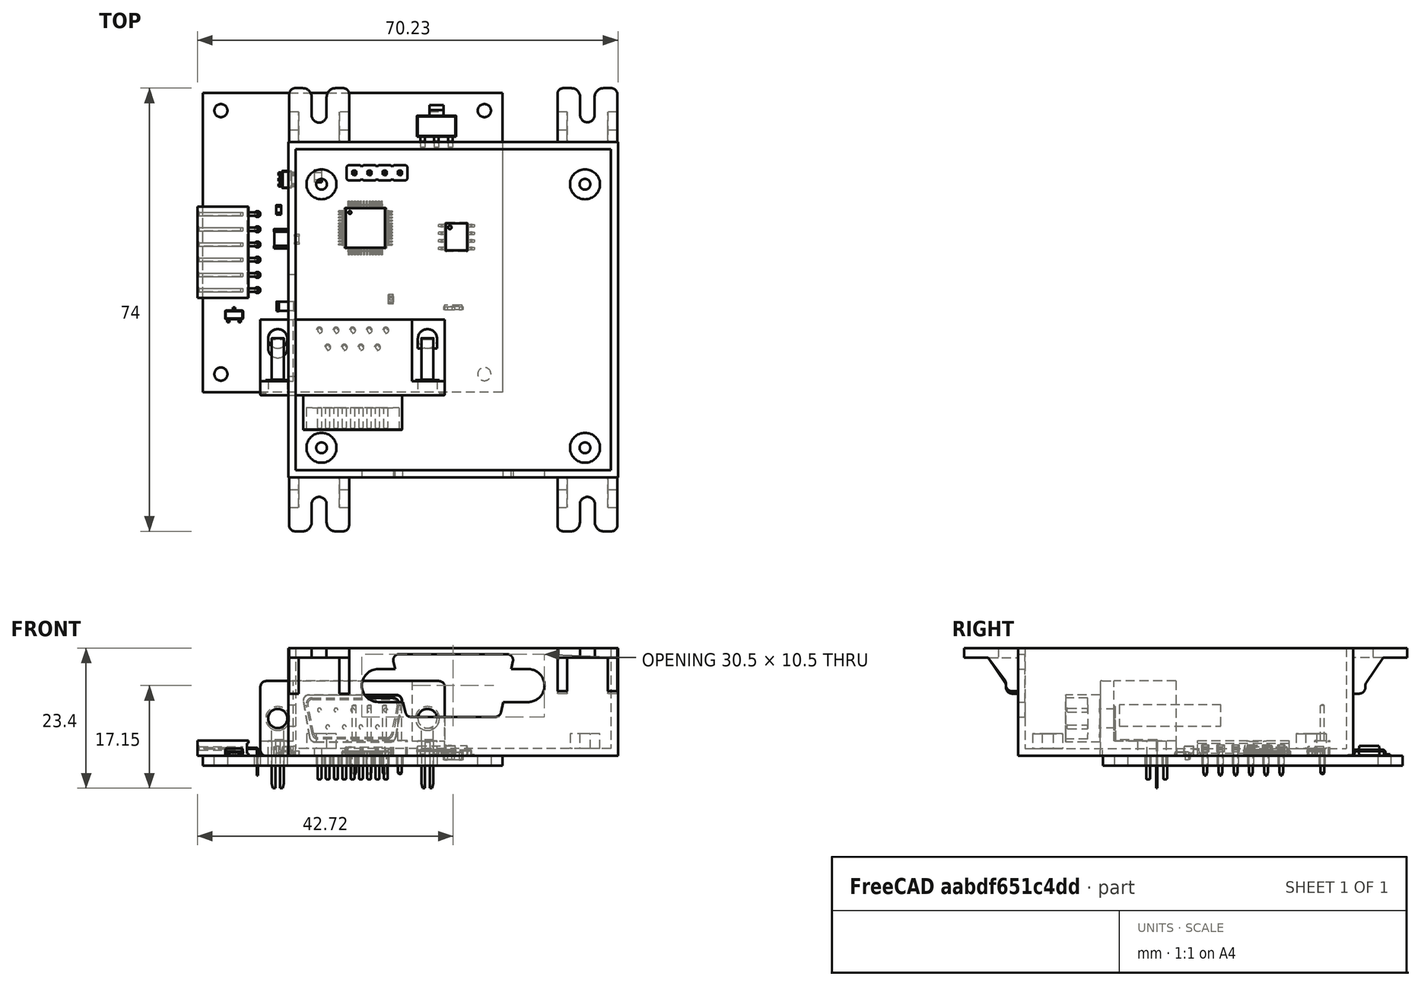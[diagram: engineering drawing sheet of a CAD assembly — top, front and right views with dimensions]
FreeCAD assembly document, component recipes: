
FREECAD ASSEMBLY — COMPONENT RECIPES ("CentralBox")

This assembly document has 6 components, labeled P0..P5 below (a component is one placed body or linked part). 5 of them carry a construction recipe — the FreeCAD feature program that regenerates the part from scratch, quoted from this document or its linked companion documents; the rest are supplied as boundary geometry only. No exploded tour is included for this assembly.
COMPONENT P0 — geometry summary ("CTB-01.kicad_pro"; no construction recipe available for this part):
  bounding box: 56.3 x 50.9 x 17.9 mm
  tessellated surface: 83,718 triangles
  volume: 7836 mm^3 (15% of its bounding box)
COMPONENT P1 — recipe-attached ("Body", modeled in this document).
Construction recipe (the document's own serialized feature program — sketch geometry with constraints, then the solid features built on it; lengths are millimeters unless a unit is written):

FEATURE [Sketcher::SketchObject] Sketch
  FullyConstrained = true
  MapMode = 2
  Support = -> [XY_Plane]
  expr: Constraints[8] = <<Params>>.box_width_external
  expr: Constraints[9] = <<Params>>.box_length_external
  sketch-geometry (4):
    g0: LineSegment StartX=-27.5 StartY=28 StartZ=0 EndX=27.5 EndY=28 EndZ=0
    g1: LineSegment StartX=27.5 StartY=28 StartZ=0 EndX=27.5 EndY=-28 EndZ=0
    g2: LineSegment StartX=27.5 StartY=-28 StartZ=0 EndX=-27.5 EndY=-28 EndZ=0
    g3: LineSegment StartX=-27.5 StartY=-28 StartZ=0 EndX=-27.5 EndY=28 EndZ=0
  constraints (10):
    c: Coincident(g0,g1)
    c: Coincident(g1,g2)
    c: Coincident(g2,g3)
    c: Coincident(g3,g0)
    c: Horizontal(g2)
    c: Vertical(g3)
    c: Symmetric(g0,g1,g-1)
    c: Symmetric(g0,g0,g-2)
    c: DistanceY(g2,g0) = 56
    c: DistanceX(g0,g0) = 55
FEATURE [PartDesign::Pad] Pad
  Direction = (0,0,1)
  Length = 18
  Length2 = 10
  Profile = -> Sketch
  ReferenceAxis = -> Sketch [N_Axis]
  Type = 0
  expr: Length = <<Params>>.box_height
FEATURE [Sketcher::SketchObject] Sketch012
  FullyConstrained = true
  MapMode = 5
  Placement = pos=(0,0,18) rot=(0,0,1;0rad)
  Support = -> [Pad]
  expr: Constraints[8] = <<Params>>.box_length_internal
  expr: Constraints[9] = <<Params>>.box_width_internal
  sketch-geometry (4):
    g0: LineSegment StartX=-26.3 StartY=26.8 StartZ=0 EndX=26.3 EndY=26.8 EndZ=0
    g1: LineSegment StartX=26.3 StartY=26.8 StartZ=0 EndX=26.3 EndY=-26.8 EndZ=0
    g2: LineSegment StartX=26.3 StartY=-26.8 StartZ=0 EndX=-26.3 EndY=-26.8 EndZ=0
    g3: LineSegment StartX=-26.3 StartY=-26.8 StartZ=0 EndX=-26.3 EndY=26.8 EndZ=0
  constraints (10):
    c: Coincident(g0,g1)
    c: Coincident(g1,g2)
    c: Coincident(g2,g3)
    c: Coincident(g3,g0)
    c: Horizontal(g2)
    c: Vertical(g1)
    c: Symmetric(g0,g0,g-2)
    c: Symmetric(g0,g2,g-1)
    c: DistanceX(g0,g0) = 52.6
    c: DistanceY(g2,g0) = 53.6
FEATURE [PartDesign::Pocket] Pocket
  BaseFeature = -> Pad
  Direction = (0,0,-1)
  Length = 16.8
  Length2 = 5
  Profile = -> Sketch012
  ReferenceAxis = -> Sketch012 [N_Axis]
  Type = 0
  expr: Length = <<Params>>.box_depth
FEATURE [PartDesign::SubShapeBinder] Binder
  BindCopyOnChange = 0
  BindMode = 0
  ClaimChildren = false
  Context = -> Body [Binder.]
  Fuse = false
  MakeFace = true
  OffsetFill = false
  OffsetIntersection = false
  OffsetJoinType = 0
  OffsetOpenResult = false
  PartialLoad = false
  Relative = true
  Support = -> [Board_1da8[Step_Models_1da8.Top_1da8.Shape011.Face27]]
  _Version = 2
FEATURE [Sketcher::SketchObject] Sketch013
  ExternalGeometry = -> [Binder]
  FullyConstrained = true
  MapMode = 5
  Placement = pos=(0,-28,0) rot=(1,0,0;1.5708rad)
  Support = -> [Pocket]
  sketch-geometry (17):
    g0: ArcOfCircle CenterX=12.49 CenterY=11.75 CenterZ=0 NormalX=0 NormalY=0 NormalZ=1 AngleXU=0 Radius=2.75 StartAngle=4.70512 EndAngle=7.85398
    g1: ArcOfCircle CenterX=-12.51 CenterY=11.75 CenterZ=0 NormalX=0 NormalY=0 NormalZ=1 AngleXU=0 Radius=2.75 StartAngle=1.5708 EndAngle=4.71239
    g2: LineSegment StartX=-12.51 StartY=9 StartZ=0 EndX=-8.39 EndY=9 EndZ=0
    g3: LineSegment StartX=-12.51 StartY=14.5 StartZ=0 EndX=-9.68 EndY=14.5 EndZ=0
    g4: LineSegment StartX=-12.51 StartY=11.75 StartZ=0 EndX=12.49 EndY=11.75 EndZ=0
    g5: ArcOfCircle CenterX=-9.01 CenterY=16 CenterZ=0 NormalX=0 NormalY=0 NormalZ=1 AngleXU=0 Radius=1 StartAngle=1.5708 EndAngle=3.37594
    g6: ArcOfCircle CenterX=8.99 CenterY=16 CenterZ=0 NormalX=0 NormalY=0 NormalZ=1 AngleXU=0 Radius=1 StartAngle=6.04884 EndAngle=7.85398
    g7: ArcOfCircle CenterX=6.99 CenterY=7.5 CenterZ=0 NormalX=0 NormalY=0 NormalZ=1 AngleXU=0 Radius=1 StartAngle=4.71239 EndAngle=6.06326
    g8: ArcOfCircle CenterX=-7.01 CenterY=7.5 CenterZ=0 NormalX=0 NormalY=0 NormalZ=1 AngleXU=0 Radius=1 StartAngle=3.37255 EndAngle=4.71239
    g9: LineSegment StartX=-9.01 StartY=17 StartZ=0 EndX=8.99 EndY=17 EndZ=0
    g10: LineSegment StartX=6.99 StartY=6.5 StartZ=0 EndX=-7.01 EndY=6.5 EndZ=0
    g11: LineSegment StartX=-7.98345 StartY=7.27109 StartZ=0 EndX=-8.39 EndY=9 EndZ=0
    g12: LineSegment StartX=7.96591 StartY=7.28184 StartZ=0 EndX=8.35 EndY=9 EndZ=0
    g13: LineSegment StartX=9.66 StartY=14.5 StartZ=0 EndX=12.49 EndY=14.5 EndZ=0
    g14: LineSegment StartX=-9.68 StartY=14.5 StartZ=0 EndX=-9.98267 EndY=15.7678 EndZ=0
    g15: LineSegment StartX=8.35 StartY=9 StartZ=0 EndX=12.47 EndY=9.00007 EndZ=0
    g16: LineSegment StartX=9.66 StartY=14.5 StartZ=0 EndX=9.96267 EndY=15.7678 EndZ=0
  constraints (44):
    c: Coincident(g0,g-4)
    c: Coincident(g1,g-3)
    c: Diameter(g1) = 5.5
    c: Equal(g1,g0)
    c: Coincident(g4,g1)
    c: Coincident(g4,g0)
    c: Diameter(g6) = 2
    c: Equal(g6,g5)
    c: Equal(g5,g8)
    c: Equal(g8,g7)
    c: Horizontal(g9)
    c: Horizontal(g10)
    c: DistanceY(g10,g9) = 10.5
    c: DistanceX(g5,g6) = 18
    c: DistanceX(g8,g7) = 14
    c: DistanceX(g7,g0) = 5.5
    c: DistanceY(g7,g0) = 4.25
    c: DistanceX(g6,g0) = 3.5
    c: Tangent(g5,g9) = 1.5708
    c: Tangent(g6,g9) = 1.5708
    c: Tangent(g7,g12) = -1.5708
    c: Tangent(g7,g10) = 1.5708
    c: Tangent(g8,g10) = 1.5708
    c: Tangent(g8,g11) = 1.5708
    c: Tangent(g1,g3) = 1.5708
    c: Tangent(g1,g2) = -1.5708
    c: Coincident(g0,g15) = -1.5708
    c: Coincident(g0,g13) = 1.5708
    c: Coincident(g14,g3)
    c: Coincident(g2,g11)
    c: Coincident(g16,g13)
    c: Coincident(g12,g15)
    c: Horizontal(g2,g12)
    c: Horizontal(g3,g13)
    c: Equal(g13,g3)
    c: Equal(g2,g15)
    c: DistanceX(g2,g2) = 4.12
    c: DistanceX(g1,g3) = 2.83
    c: DistanceY(g1,g3) = 2.75
    c: DistanceY(g2,g1) = 2.75
    c: DistanceX(g13,g0) = 2.83
    c: DistanceX(g12,g0) = 4.14
    c: Tangent(g5,g14) = 1.5708
    c: Tangent(g6,g16) = -1.5708
FEATURE [PartDesign::Pocket] Pocket001
  BaseFeature = -> Pocket
  Direction = (0,1,-2e-16)
  Length = 5
  Length2 = 5
  Profile = -> Sketch013
  ReferenceAxis = -> Sketch013 [N_Axis]
  Type = 2
FEATURE [Sketcher::SketchObject] Sketch014
  FullyConstrained = true
  MapMode = 5
  Placement = pos=(-27.5,0,0) rot=(0.57735,-0.57735,-0.57735;2.0944rad)
  Support = -> [Pocket001]
  expr: Constraints[10] = <<Params>>.side_window_height
  expr: Constraints[11] = <<Params>>.side_window_y
  expr: Constraints[8] = <<Params>>.side_window_length
  expr: Constraints[9] = <<Params>>.side_window_z
  sketch-geometry (4):
    g0: LineSegment StartX=-5.9 StartY=8.5 StartZ=0 EndX=11.1 EndY=8.5 EndZ=0
    g1: LineSegment StartX=11.1 StartY=8.5 StartZ=0 EndX=11.1 EndY=5 EndZ=0
    g2: LineSegment StartX=11.1 StartY=5 StartZ=0 EndX=-5.9 EndY=5 EndZ=0
    g3: LineSegment StartX=-5.9 StartY=5 StartZ=0 EndX=-5.9 EndY=8.5 EndZ=0
  constraints (12):
    c: Coincident(g0,g1)
    c: Coincident(g1,g2)
    c: Coincident(g2,g3)
    c: Coincident(g3,g0)
    c: Horizontal(g0)
    c: Horizontal(g2)
    c: Vertical(g1)
    c: Vertical(g3)
    c: DistanceX(g2,g1) = 17
    c: DistanceY(g-1,g2) = 5
    c: DistanceY(g2,g0) = 3.5
    c: DistanceX(g-1,g1) = 11.1
FEATURE [PartDesign::Pocket] Pocket002
  BaseFeature = -> Pocket001
  Direction = (1,0,0)
  Length = 5
  Length2 = 5
  Profile = -> Sketch014
  ReferenceAxis = -> Sketch014 [N_Axis]
  Type = 2
FEATURE [PartDesign::SubShapeBinder] Binder001
  BindCopyOnChange = 0
  BindMode = 0
  ClaimChildren = false
  Context = -> Body [Binder001.]
  Fuse = false
  MakeFace = true
  OffsetFill = false
  OffsetIntersection = false
  OffsetJoinType = 0
  OffsetOpenResult = false
  PartialLoad = false
  Relative = true
  Support = -> [Board_1da8[Board_Geoms_1da8.Pcb_1da8.]]
  _Version = 2
FEATURE [Sketcher::SketchObject] Sketch015
  ExternalGeometry = -> [Binder001]
  FullyConstrained = true
  MapMode = 5
  Placement = pos=(0,0,1.2) rot=(0,0,1;0rad)
  Support = -> [Pocket002]
  expr: Constraints[8] = <<Params>>.monting_boss_hole
  expr: Constraints[9] = <<Params>>.mounting_boss_pad
  sketch-geometry (8):
    g0: Circle CenterX=22 CenterY=-23.05 CenterZ=0 NormalX=0 NormalY=0 NormalZ=1 AngleXU=0 Radius=0.9
    g1: Circle CenterX=22 CenterY=-23.05 CenterZ=0 NormalX=0 NormalY=0 NormalZ=1 AngleXU=0 Radius=2.5
    g2: Circle CenterX=-22 CenterY=-23.05 CenterZ=0 NormalX=0 NormalY=0 NormalZ=1 AngleXU=0 Radius=0.9
    g3: Circle CenterX=-22 CenterY=-23.05 CenterZ=0 NormalX=0 NormalY=0 NormalZ=1 AngleXU=0 Radius=2.5
    g4: Circle CenterX=22 CenterY=20.95 CenterZ=0 NormalX=0 NormalY=0 NormalZ=1 AngleXU=0 Radius=0.9
    g5: Circle CenterX=22 CenterY=20.95 CenterZ=0 NormalX=0 NormalY=0 NormalZ=1 AngleXU=0 Radius=2.5
    g6: Circle CenterX=-22 CenterY=20.95 CenterZ=0 NormalX=0 NormalY=0 NormalZ=1 AngleXU=0 Radius=0.9
    g7: Circle CenterX=-22 CenterY=20.95 CenterZ=0 NormalX=0 NormalY=0 NormalZ=1 AngleXU=0 Radius=2.5
  constraints (16):
    c: Coincident(g0,g-5)
    c: Coincident(g1,g0)
    c: Coincident(g2,g-6)
    c: Coincident(g3,g2)
    c: Coincident(g4,g-4)
    c: Coincident(g5,g4)
    c: Coincident(g6,g-3)
    c: Coincident(g7,g6)
    c: Diameter(g4) = 1.8
    c: Diameter(g5) = 5
    c: Equal(g4,g2)
    c: Equal(g2,g0)
    c: Equal(g4,g6)
    c: Equal(g5,g7)
    c: Equal(g7,g1)
    c: Equal(g1,g3)
FEATURE [PartDesign::Pad] Pad010
  BaseFeature = -> Pocket002
  Direction = (0,0,1)
  Length = 2.5
  Length2 = 10
  Profile = -> Sketch015
  ReferenceAxis = -> Sketch015 [N_Axis]
  Type = 0
  expr: Length = <<Params>>.mounting_boss_height
FEATURE [PartDesign::Body] Body
  Group = -> [Sketch,Pad,Sketch012,Pocket,Binder,Sketch013,Pocket001,Sketch014,Pocket002,Binder001,Sketch015,Pad010]
  Origin = -> Origin
  Tip = -> Pad010
COMPONENT P2 — recipe-attached ("Tab1", modeled in this document).
Construction recipe (the document's own serialized feature program — sketch geometry with constraints, then the solid features built on it; lengths are millimeters unless a unit is written):

FEATURE [Sketcher::SketchObject] Sketch004
  FullyConstrained = true
  MapMode = 5
  Support = -> [XY_Plane009]
  expr: Constraints[13] = <<Params001>>.tab_length
  expr: Constraints[14] = <<Params001>>.tab_width
  expr: Constraints[19] = <<Params001>>.tab_hole_diameter
  expr: Constraints[20] = <<Params001>>.tab_hole_x
  sketch-geometry (8):
    g0: LineSegment StartX=-4.5 StartY=5 StartZ=0 EndX=4.5 EndY=5 EndZ=0
    g1: LineSegment StartX=4.5 StartY=5 StartZ=0 EndX=4.5 EndY=1.25 EndZ=0
    g2: LineSegment StartX=4.5 StartY=-5 StartZ=0 EndX=-4.5 EndY=-5 EndZ=0
    g3: LineSegment StartX=-4.5 StartY=-5 StartZ=0 EndX=-4.5 EndY=5 EndZ=0
    g4: ArcOfCircle CenterX=-1e-16 CenterY=0 CenterZ=0 NormalX=0 NormalY=0 NormalZ=1 AngleXU=0 Radius=1.25 StartAngle=1.5708 EndAngle=4.71239
    g5: LineSegment StartX=-3e-16 StartY=1.25 StartZ=0 EndX=4.5 EndY=1.25 EndZ=0
    g6: LineSegment StartX=4.5 StartY=-1.25 StartZ=0 EndX=0 EndY=-1.25 EndZ=0
    g7: LineSegment StartX=4.5 StartY=-1.25 StartZ=0 EndX=4.5 EndY=-5 EndZ=0
  constraints (21):
    c: Coincident(g0,g1)
    c: Coincident(g7,g2)
    c: Coincident(g2,g3)
    c: Coincident(g3,g0)
    c: Horizontal(g2)
    c: Vertical(g1)
    c: Symmetric(g0,g0,g-2)
    c: Symmetric(g0,g2,g-1)
    c: PointOnObject(g4,g-1)
    c: Horizontal(g5)
    c: Horizontal(g6)
    c: Coincident(g1,g5)
    c: Coincident(g7,g6)
    c: DistanceX(g0,g0) = 9
    c: DistanceY(g2,g0) = 10
    c: Tangent(g4,g5) = 1.5708
    c: Tangent(g6,g4) = 1.5708
    c: Vertical(g7)
    c: Vertical(g6,g1)
    c: Diameter(g4) = 2.5
    c: DistanceX(g0,g4) = 4.5
FEATURE [PartDesign::Pad] Pad002
  Direction = (0,0,1)
  Length = 1.6
  Length2 = 10
  Profile = -> Sketch004
  ReferenceAxis = -> Sketch004 [N_Axis]
  Type = 0
  expr: Length = <<Params001>>.tab_thickness
FEATURE [PartDesign::Plane] DatumPlane002  label="PlaneRib"
  Length = 60
  MapMode = 5
  Placement = pos=(0,-5,0) rot=(1,0,0;1.5708rad)
  ResizeMode = 0
  Support = -> [Pad002]
  Width = 60
FEATURE [Sketcher::SketchObject] Sketch005
  ExternalGeometry = -> [Pad002]
  FullyConstrained = true
  MapMode = 5
  Placement = pos=(0,-5,0) rot=(1,0,0;1.5708rad)
  Support = -> [DatumPlane002]
  expr: Constraints[11] = <<Params001>>.tab_rib_height
  expr: Constraints[12] = <<Params001>>.tab_rib_length
  expr: Constraints[13] = <<Params001>>.tab_rib_insert
  expr: Constraints[6] = <<Params001>>.tab_height
  sketch-geometry (5):
    g0: LineSegment StartX=-4.5 StartY=0 StartZ=0 EndX=-4.5 EndY=-5.6 EndZ=0
    g1: LineSegment StartX=-4.5 StartY=-5.6 StartZ=0 EndX=-2.5 EndY=-5.6 EndZ=0
    g2: LineSegment StartX=0.5 StartY=0 StartZ=0 EndX=-4.5 EndY=0 EndZ=0
    g3: LineSegment StartX=-2.5 StartY=-5.6 StartZ=0 EndX=-2.5 EndY=-4 EndZ=0
    g4: LineSegment StartX=-2.5 StartY=-4 StartZ=0 EndX=0.5 EndY=0 EndZ=0
  constraints (14):
    c: Coincident(g0,g-3)
    c: Vertical(g0)
    c: Coincident(g1,g0)
    c: PointOnObject(g2,g-1)
    c: Coincident(g2,g0)
    c: Horizontal(g1)
    c: DistanceY(g0,g0) = 5.6
    c: Coincident(g3,g1)
    c: Vertical(g3)
    c: Coincident(g4,g3)
    c: Coincident(g4,g2)
    c: DistanceY(g3,g-1) = 4
    c: DistanceX(g0,g2) = 5
    c: DistanceX(g0,g1) = 2
FEATURE [PartDesign::Pad] Pad003  label="TabRib1"
  BaseFeature = -> Pad002
  Direction = (0,-1,2e-16)
  Length = 1.6
  Length2 = 10
  Profile = -> Sketch005
  ReferenceAxis = -> Sketch005 [N_Axis]
  Reversed = true
  Type = 0
  expr: Length = <<Params001>>.tab_rib_thickness
FEATURE [PartDesign::LinearPattern] LinearPattern  label="TabRib2"
  BaseFeature = -> Pad003
  Direction = -> Y_Axis009
  Length = 8.4
  Occurrences = 2
  Originals = -> [Pad003]
  expr: Length = <<Params001>>.tab_ribs_gap
FEATURE [PartDesign::Fillet] Fillet
  Base = -> LinearPattern [Edge51,Edge52]
  BaseFeature = -> LinearPattern
  Radius = 1
  SupportTransform = false
  UseAllEdges = false
FEATURE [PartDesign::Fillet] Fillet001
  Base = -> Fillet [Edge14,Edge52]
  BaseFeature = -> Fillet
  Radius = 1
  SupportTransform = false
  UseAllEdges = false
FEATURE [PartDesign::Fillet] Fillet002
  Base = -> Fillet001 [Edge19,Edge53]
  BaseFeature = -> Fillet001
  Radius = 1
  SupportTransform = false
  UseAllEdges = false
FEATURE [PartDesign::Fillet] Fillet003
  Base = -> Fillet002 [Edge38,Edge43]
  BaseFeature = -> Fillet002
  Radius = 1.5
  SupportTransform = false
  UseAllEdges = false
FEATURE [PartDesign::Body] Body001  label="Tab1"
  Group = -> [Sketch004,Pad002,DatumPlane002,Sketch005,Pad003,LinearPattern,Fillet,Fillet001,Fillet002,Fillet003]
  Origin = -> Origin009
  Placement = pos=(22.4,-32.5,16.4) rot=(0,0,-1;1.5708rad)
  Tip = -> Fillet003
COMPONENT P3 — recipe-attached ("Tab2", modeled in this document).
Construction recipe (the document's own serialized feature program — sketch geometry with constraints, then the solid features built on it; lengths are millimeters unless a unit is written):

FEATURE [Sketcher::SketchObject] Sketch006
  FullyConstrained = true
  MapMode = 5
  Support = -> [XY_Plane010]
  expr: Constraints[13] = <<Params002>>.tab_length
  expr: Constraints[14] = <<Params002>>.tab_width
  expr: Constraints[19] = <<Params002>>.tab_hole_diameter
  expr: Constraints[20] = <<Params002>>.tab_hole_x
  sketch-geometry (8):
    g0: LineSegment StartX=-4.5 StartY=5 StartZ=0 EndX=4.5 EndY=5 EndZ=0
    g1: LineSegment StartX=4.5 StartY=5 StartZ=0 EndX=4.5 EndY=1.2 EndZ=0
    g2: LineSegment StartX=4.5 StartY=-5 StartZ=0 EndX=-4.5 EndY=-5 EndZ=0
    g3: LineSegment StartX=-4.5 StartY=-5 StartZ=0 EndX=-4.5 EndY=5 EndZ=0
    g4: ArcOfCircle CenterX=-3e-16 CenterY=0 CenterZ=0 NormalX=0 NormalY=0 NormalZ=1 AngleXU=0 Radius=1.2 StartAngle=1.5708 EndAngle=4.71239
    g5: LineSegment StartX=-5e-16 StartY=1.2 StartZ=0 EndX=4.5 EndY=1.2 EndZ=0
    g6: LineSegment StartX=4.5 StartY=-1.2 StartZ=0 EndX=-9e-16 EndY=-1.2 EndZ=0
    g7: LineSegment StartX=4.5 StartY=-1.2 StartZ=0 EndX=4.5 EndY=-5 EndZ=0
  constraints (21):
    c: Coincident(g0,g1)
    c: Coincident(g7,g2)
    c: Coincident(g2,g3)
    c: Coincident(g3,g0)
    c: Horizontal(g2)
    c: Vertical(g1)
    c: Symmetric(g0,g0,g-2)
    c: Symmetric(g0,g2,g-1)
    c: PointOnObject(g4,g-1)
    c: Horizontal(g5)
    c: Horizontal(g6)
    c: Coincident(g1,g5)
    c: Coincident(g7,g6)
    c: DistanceX(g0,g0) = 9
    c: DistanceY(g2,g0) = 10
    c: Tangent(g4,g5) = 1.5708
    c: Tangent(g6,g4) = 1.5708
    c: Vertical(g7)
    c: Vertical(g6,g1)
    c: Diameter(g4) = 2.4
    c: DistanceX(g0,g4) = 4.5
FEATURE [PartDesign::Pad] Pad004
  Direction = (0,0,1)
  Length = 1.6
  Length2 = 10
  Profile = -> Sketch006
  ReferenceAxis = -> Sketch006 [N_Axis]
  Type = 0
  expr: Length = <<Params002>>.tab_thickness
FEATURE [PartDesign::Plane] DatumPlane003  label="PlaneRib001"
  Length = 60
  MapMode = 5
  Placement = pos=(0,-5,0) rot=(1,0,0;1.5708rad)
  ResizeMode = 0
  Support = -> [Pad004]
  Width = 60
FEATURE [Sketcher::SketchObject] Sketch007
  ExternalGeometry = -> [Pad004]
  FullyConstrained = true
  MapMode = 5
  Placement = pos=(0,-5,0) rot=(1,0,0;1.5708rad)
  Support = -> [DatumPlane003]
  expr: Constraints[11] = <<Params002>>.tab_rib_height
  expr: Constraints[12] = <<Params002>>.tab_rib_length
  expr: Constraints[13] = <<Params002>>.tab_rib_insert
  expr: Constraints[6] = <<Params002>>.tab_height
  sketch-geometry (5):
    g0: LineSegment StartX=-4.5 StartY=0 StartZ=0 EndX=-4.5 EndY=-6 EndZ=0
    g1: LineSegment StartX=-4.5 StartY=-6 StartZ=0 EndX=-2.5 EndY=-6 EndZ=0
    g2: LineSegment StartX=0.5 StartY=0 StartZ=0 EndX=-4.5 EndY=0 EndZ=0
    g3: LineSegment StartX=-2.5 StartY=-6 StartZ=0 EndX=-2.5 EndY=-4.4 EndZ=0
    g4: LineSegment StartX=-2.5 StartY=-4.4 StartZ=0 EndX=0.5 EndY=0 EndZ=0
  constraints (14):
    c: Coincident(g0,g-3)
    c: Vertical(g0)
    c: Coincident(g1,g0)
    c: PointOnObject(g2,g-1)
    c: Coincident(g2,g0)
    c: Horizontal(g1)
    c: DistanceY(g0,g0) = 6
    c: Coincident(g3,g1)
    c: Vertical(g3)
    c: Coincident(g4,g3)
    c: Coincident(g4,g2)
    c: DistanceY(g3,g-1) = 4.4
    c: DistanceX(g0,g2) = 5
    c: DistanceX(g0,g1) = 2
FEATURE [PartDesign::Pad] Pad005  label="TabRib004"
  BaseFeature = -> Pad004
  Direction = (0,-1,2e-16)
  Length = 1.6
  Length2 = 10
  Profile = -> Sketch007
  ReferenceAxis = -> Sketch007 [N_Axis]
  Reversed = true
  Type = 0
  expr: Length = <<Params002>>.tab_rib_thickness
FEATURE [PartDesign::LinearPattern] LinearPattern001  label="TabRib003"
  BaseFeature = -> Pad005
  Direction = -> Y_Axis010
  Length = 8.4
  Occurrences = 2
  Originals = -> [Pad005]
  expr: Length = <<Params002>>.tab_ribs_gap
FEATURE [PartDesign::Fillet] Fillet004
  Base = -> LinearPattern001 [Edge51,Edge52]
  BaseFeature = -> LinearPattern001
  Radius = 1
  SupportTransform = false
  UseAllEdges = false
FEATURE [PartDesign::Fillet] Fillet005
  Base = -> Fillet004 [Edge14,Edge52]
  BaseFeature = -> Fillet004
  Radius = 1
  SupportTransform = false
  UseAllEdges = false
FEATURE [PartDesign::Fillet] Fillet006
  Base = -> Fillet005 [Edge19,Edge53]
  BaseFeature = -> Fillet005
  Radius = 1
  SupportTransform = false
  UseAllEdges = false
FEATURE [PartDesign::Fillet] Fillet007
  Base = -> Fillet006 [Edge38,Edge43]
  BaseFeature = -> Fillet006
  Radius = 1.5
  SupportTransform = false
  UseAllEdges = false
FEATURE [PartDesign::Body] Body002  label="Tab2"
  Group = -> [Sketch006,Pad004,DatumPlane003,Sketch007,Pad005,LinearPattern001,Fillet004,Fillet005,Fillet006,Fillet007]
  Origin = -> Origin010
  Placement = pos=(22.4,32.5,16.4) rot=(0,0,1;1.5708rad)
  Tip = -> Fillet007
COMPONENT P4 — recipe-attached ("Tab3", modeled in this document).
Construction recipe (the document's own serialized feature program — sketch geometry with constraints, then the solid features built on it; lengths are millimeters unless a unit is written):

FEATURE [Sketcher::SketchObject] Sketch008
  FullyConstrained = true
  MapMode = 5
  Support = -> [XY_Plane011]
  expr: Constraints[13] = <<Params003>>.tab_length
  expr: Constraints[14] = <<Params003>>.tab_width
  expr: Constraints[19] = <<Params003>>.tab_hole_diameter
  expr: Constraints[20] = <<Params003>>.tab_hole_x
  sketch-geometry (8):
    g0: LineSegment StartX=-4.5 StartY=5 StartZ=0 EndX=4.5 EndY=5 EndZ=0
    g1: LineSegment StartX=4.5 StartY=5 StartZ=0 EndX=4.5 EndY=1.25 EndZ=0
    g2: LineSegment StartX=4.5 StartY=-5 StartZ=0 EndX=-4.5 EndY=-5 EndZ=0
    g3: LineSegment StartX=-4.5 StartY=-5 StartZ=0 EndX=-4.5 EndY=5 EndZ=0
    g4: ArcOfCircle CenterX=-1e-16 CenterY=0 CenterZ=0 NormalX=0 NormalY=0 NormalZ=1 AngleXU=0 Radius=1.25 StartAngle=1.5708 EndAngle=4.71239
    g5: LineSegment StartX=-3e-16 StartY=1.25 StartZ=0 EndX=4.5 EndY=1.25 EndZ=0
    g6: LineSegment StartX=4.5 StartY=-1.25 StartZ=0 EndX=0 EndY=-1.25 EndZ=0
    g7: LineSegment StartX=4.5 StartY=-1.25 StartZ=0 EndX=4.5 EndY=-5 EndZ=0
  constraints (21):
    c: Coincident(g0,g1)
    c: Coincident(g7,g2)
    c: Coincident(g2,g3)
    c: Coincident(g3,g0)
    c: Horizontal(g2)
    c: Vertical(g1)
    c: Symmetric(g0,g0,g-2)
    c: Symmetric(g0,g2,g-1)
    c: PointOnObject(g4,g-1)
    c: Horizontal(g5)
    c: Horizontal(g6)
    c: Coincident(g1,g5)
    c: Coincident(g7,g6)
    c: DistanceX(g0,g0) = 9
    c: DistanceY(g2,g0) = 10
    c: Tangent(g4,g5) = 1.5708
    c: Tangent(g6,g4) = 1.5708
    c: Vertical(g7)
    c: Vertical(g6,g1)
    c: Diameter(g4) = 2.5
    c: DistanceX(g0,g4) = 4.5
FEATURE [PartDesign::Pad] Pad006
  Direction = (0,0,1)
  Length = 1.6
  Length2 = 10
  Profile = -> Sketch008
  ReferenceAxis = -> Sketch008 [N_Axis]
  Type = 0
  expr: Length = <<Params003>>.tab_thickness
FEATURE [PartDesign::Plane] DatumPlane004  label="PlaneRib002"
  Length = 60
  MapMode = 5
  Placement = pos=(0,-5,0) rot=(1,0,0;1.5708rad)
  ResizeMode = 0
  Support = -> [Pad006]
  Width = 60
FEATURE [Sketcher::SketchObject] Sketch009
  ExternalGeometry = -> [Pad006]
  FullyConstrained = true
  MapMode = 5
  Placement = pos=(0,-5,0) rot=(1,0,0;1.5708rad)
  Support = -> [DatumPlane004]
  expr: Constraints[11] = <<Params003>>.tab_rib_height
  expr: Constraints[12] = <<Params003>>.tab_rib_length
  expr: Constraints[13] = <<Params003>>.tab_rib_insert
  expr: Constraints[6] = <<Params003>>.tab_height
  sketch-geometry (5):
    g0: LineSegment StartX=-4.5 StartY=0 StartZ=0 EndX=-4.5 EndY=-6 EndZ=0
    g1: LineSegment StartX=-4.5 StartY=-6 StartZ=0 EndX=-2.5 EndY=-6 EndZ=0
    g2: LineSegment StartX=0.5 StartY=0 StartZ=0 EndX=-4.5 EndY=0 EndZ=0
    g3: LineSegment StartX=-2.5 StartY=-6 StartZ=0 EndX=-2.5 EndY=-4.4 EndZ=0
    g4: LineSegment StartX=-2.5 StartY=-4.4 StartZ=0 EndX=0.5 EndY=0 EndZ=0
  constraints (14):
    c: Coincident(g0,g-3)
    c: Vertical(g0)
    c: Coincident(g1,g0)
    c: PointOnObject(g2,g-1)
    c: Coincident(g2,g0)
    c: Horizontal(g1)
    c: DistanceY(g0,g0) = 6
    c: Coincident(g3,g1)
    c: Vertical(g3)
    c: Coincident(g4,g3)
    c: Coincident(g4,g2)
    c: DistanceY(g3,g-1) = 4.4
    c: DistanceX(g0,g2) = 5
    c: DistanceX(g0,g1) = 2
FEATURE [PartDesign::Pad] Pad007  label="TabRib006"
  BaseFeature = -> Pad006
  Direction = (0,-1,2e-16)
  Length = 1.6
  Length2 = 10
  Profile = -> Sketch009
  ReferenceAxis = -> Sketch009 [N_Axis]
  Reversed = true
  Type = 0
  expr: Length = <<Params003>>.tab_rib_thickness
FEATURE [PartDesign::LinearPattern] LinearPattern002  label="TabRib005"
  BaseFeature = -> Pad007
  Direction = -> Y_Axis011
  Length = 8.4
  Occurrences = 2
  Originals = -> [Pad007]
  expr: Length = <<Params003>>.tab_ribs_gap
FEATURE [PartDesign::Fillet] Fillet008
  Base = -> LinearPattern002 [Edge51,Edge52]
  BaseFeature = -> LinearPattern002
  Radius = 1
  SupportTransform = false
  UseAllEdges = false
FEATURE [PartDesign::Fillet] Fillet009
  Base = -> Fillet008 [Edge14,Edge52]
  BaseFeature = -> Fillet008
  Radius = 1
  SupportTransform = false
  UseAllEdges = false
FEATURE [PartDesign::Fillet] Fillet010
  Base = -> Fillet009 [Edge19,Edge53]
  BaseFeature = -> Fillet009
  Radius = 1
  SupportTransform = false
  UseAllEdges = false
FEATURE [PartDesign::Fillet] Fillet011
  Base = -> Fillet010 [Edge38,Edge43]
  BaseFeature = -> Fillet010
  Radius = 1.5
  SupportTransform = false
  UseAllEdges = false
FEATURE [PartDesign::Body] Body003  label="Tab3"
  Group = -> [Sketch008,Pad006,DatumPlane004,Sketch009,Pad007,LinearPattern002,Fillet008,Fillet009,Fillet010,Fillet011]
  Origin = -> Origin011
  Placement = pos=(-22.4,32.5,16.4) rot=(0,0,1;1.5708rad)
  Tip = -> Fillet011
COMPONENT P5 — recipe-attached ("Tab4", modeled in this document).
Construction recipe (the document's own serialized feature program — sketch geometry with constraints, then the solid features built on it; lengths are millimeters unless a unit is written):

FEATURE [Sketcher::SketchObject] Sketch010
  FullyConstrained = true
  MapMode = 5
  Support = -> [XY_Plane012]
  expr: Constraints[13] = <<Params004>>.tab_length
  expr: Constraints[14] = <<Params004>>.tab_width
  expr: Constraints[19] = <<Params004>>.tab_hole_diameter
  expr: Constraints[20] = <<Params004>>.tab_hole_x
  sketch-geometry (8):
    g0: LineSegment StartX=-4.5 StartY=5 StartZ=0 EndX=4.5 EndY=5 EndZ=0
    g1: LineSegment StartX=4.5 StartY=5 StartZ=0 EndX=4.5 EndY=1.25 EndZ=0
    g2: LineSegment StartX=4.5 StartY=-5 StartZ=0 EndX=-4.5 EndY=-5 EndZ=0
    g3: LineSegment StartX=-4.5 StartY=-5 StartZ=0 EndX=-4.5 EndY=5 EndZ=0
    g4: ArcOfCircle CenterX=-3e-16 CenterY=0 CenterZ=0 NormalX=0 NormalY=0 NormalZ=1 AngleXU=0 Radius=1.25 StartAngle=1.5708 EndAngle=4.71239
    g5: LineSegment StartX=-5e-16 StartY=1.25 StartZ=0 EndX=4.5 EndY=1.25 EndZ=0
    g6: LineSegment StartX=4.5 StartY=-1.25 StartZ=0 EndX=-9e-16 EndY=-1.25 EndZ=0
    g7: LineSegment StartX=4.5 StartY=-1.25 StartZ=0 EndX=4.5 EndY=-5 EndZ=0
  constraints (21):
    c: Coincident(g0,g1)
    c: Coincident(g7,g2)
    c: Coincident(g2,g3)
    c: Coincident(g3,g0)
    c: Horizontal(g2)
    c: Vertical(g1)
    c: Symmetric(g0,g0,g-2)
    c: Symmetric(g0,g2,g-1)
    c: PointOnObject(g4,g-1)
    c: Horizontal(g5)
    c: Horizontal(g6)
    c: Coincident(g1,g5)
    c: Coincident(g7,g6)
    c: DistanceX(g0,g0) = 9
    c: DistanceY(g2,g0) = 10
    c: Tangent(g4,g5) = 1.5708
    c: Tangent(g6,g4) = 1.5708
    c: Vertical(g7)
    c: Vertical(g6,g1)
    c: Diameter(g4) = 2.5
    c: DistanceX(g0,g4) = 4.5
FEATURE [PartDesign::Pad] Pad008
  Direction = (0,0,1)
  Length = 1.6
  Length2 = 10
  Profile = -> Sketch010
  ReferenceAxis = -> Sketch010 [N_Axis]
  Type = 0
  expr: Length = <<Params004>>.tab_thickness
FEATURE [PartDesign::Plane] DatumPlane005  label="PlaneRib003"
  Length = 60
  MapMode = 5
  Placement = pos=(0,-5,0) rot=(1,0,0;1.5708rad)
  ResizeMode = 0
  Support = -> [Pad008]
  Width = 60
FEATURE [Sketcher::SketchObject] Sketch011
  ExternalGeometry = -> [Pad008]
  FullyConstrained = true
  MapMode = 5
  Placement = pos=(0,-5,0) rot=(1,0,0;1.5708rad)
  Support = -> [DatumPlane005]
  expr: Constraints[11] = <<Params004>>.tab_rib_height
  expr: Constraints[12] = <<Params004>>.tab_rib_length
  expr: Constraints[13] = <<Params004>>.tab_rib_insert
  expr: Constraints[6] = <<Params004>>.tab_height
  sketch-geometry (5):
    g0: LineSegment StartX=-4.5 StartY=0 StartZ=0 EndX=-4.5 EndY=-6 EndZ=0
    g1: LineSegment StartX=-4.5 StartY=-6 StartZ=0 EndX=-2.5 EndY=-6 EndZ=0
    g2: LineSegment StartX=0.5 StartY=0 StartZ=0 EndX=-4.5 EndY=0 EndZ=0
    g3: LineSegment StartX=-2.5 StartY=-6 StartZ=0 EndX=-2.5 EndY=-4.4 EndZ=0
    g4: LineSegment StartX=-2.5 StartY=-4.4 StartZ=0 EndX=0.5 EndY=0 EndZ=0
  constraints (14):
    c: Coincident(g0,g-3)
    c: Vertical(g0)
    c: Coincident(g1,g0)
    c: PointOnObject(g2,g-1)
    c: Coincident(g2,g0)
    c: Horizontal(g1)
    c: DistanceY(g0,g0) = 6
    c: Coincident(g3,g1)
    c: Vertical(g3)
    c: Coincident(g4,g3)
    c: Coincident(g4,g2)
    c: DistanceY(g3,g-1) = 4.4
    c: DistanceX(g0,g2) = 5
    c: DistanceX(g0,g1) = 2
FEATURE [PartDesign::Pad] Pad009  label="TabRib008"
  BaseFeature = -> Pad008
  Direction = (0,-1,2e-16)
  Length = 1.6
  Length2 = 10
  Profile = -> Sketch011
  ReferenceAxis = -> Sketch011 [N_Axis]
  Reversed = true
  Type = 0
  expr: Length = <<Params004>>.tab_rib_thickness
FEATURE [PartDesign::LinearPattern] LinearPattern003  label="TabRib007"
  BaseFeature = -> Pad009
  Direction = -> Y_Axis012
  Length = 8.4
  Occurrences = 2
  Originals = -> [Pad009]
  expr: Length = <<Params004>>.tab_ribs_gap
FEATURE [PartDesign::Fillet] Fillet012
  Base = -> LinearPattern003 [Edge51,Edge52]
  BaseFeature = -> LinearPattern003
  Radius = 1
  SupportTransform = false
  UseAllEdges = false
FEATURE [PartDesign::Fillet] Fillet013
  Base = -> Fillet012 [Edge14,Edge52]
  BaseFeature = -> Fillet012
  Radius = 1
  SupportTransform = false
  UseAllEdges = false
FEATURE [PartDesign::Fillet] Fillet014
  Base = -> Fillet013 [Edge19,Edge53]
  BaseFeature = -> Fillet013
  Radius = 1
  SupportTransform = false
  UseAllEdges = false
FEATURE [PartDesign::Fillet] Fillet015
  Base = -> Fillet014 [Edge38,Edge43]
  BaseFeature = -> Fillet014
  Radius = 1.5
  SupportTransform = false
  UseAllEdges = false
FEATURE [PartDesign::Body] Body004  label="Tab4"
  Group = -> [Sketch010,Pad008,DatumPlane005,Sketch011,Pad009,LinearPattern003,Fillet012,Fillet013,Fillet014,Fillet015]
  Origin = -> Origin012
  Placement = pos=(-22.4,-32.5,16.4) rot=(0,0,-1;1.5708rad)
  Tip = -> Fillet015
PROVENANCE & LICENSES
A FreeCAD (.FCStd) document from a public repository crawl; recipes are the document's own serialized feature recipes (and, for linked parts, companion documents' recipes).
License: as declared in the source repository (recorded in the dataset sidecar).
